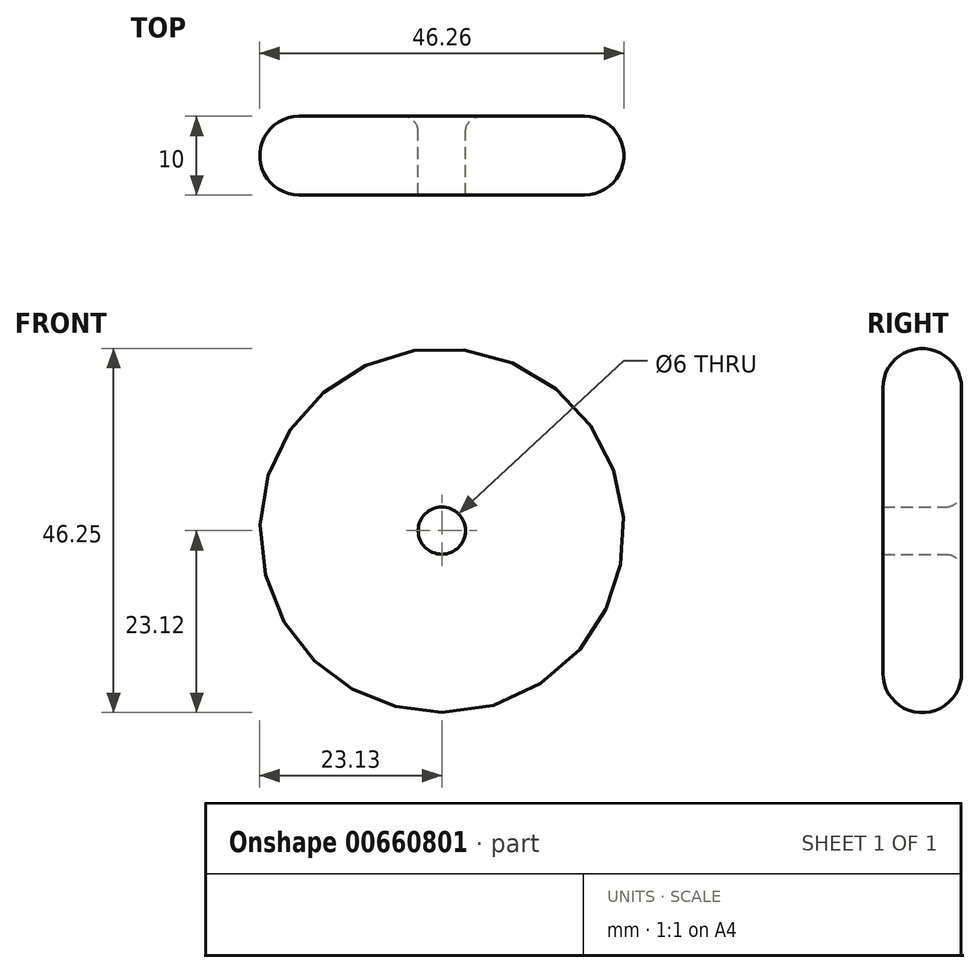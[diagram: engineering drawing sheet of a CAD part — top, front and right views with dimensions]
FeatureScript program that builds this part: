
annotation { "Feature Type Name" : "Feature", "Feature Type Description" : "" }
export const myFeature = defineFeature(function(context is Context, id is Id, definition is map)
    precondition{}
    {
        {
            var Q0;
            Q0=qCreatedBy(makeId("Front.planeOp"),FACE);
            var sketch = newSketch(context, id + "F0", { "sketchPlane" : qUnion([Q0])});
            skCircle(sketch, "E0", {"center": v(0, 0) * mm, "radius": 23.12 * mm});
            skCircle(sketch, "E1", {"center": v(0, 0) * mm, "radius": 3 * mm});
            skSolve(sketch);
        }
        {
            var Q0;
            Q0=makeQuery(id+"F0.imprint","IMPRINT",FACE,{"disambiguationData":[TD([[makeQuery(id+"F0.imprint","IMPRINT",EDGE,{"derivedFrom":sQuery(id+"F0.wireOp",EDGE,"E0")}),1.0]])]});
            extrude(context, id + "F1", {"entities" : qUnion([Q0]), "depth" : 10 * mm, "offsetDistance" : 25 * mm});
        }
        {
            var Q0;
            Q0=makeQuery(id+"F1.opExtrude","CAP_EDGE",EDGE,{"disambiguationData":[OSD([sQuery(id+"F0.wireOp",EDGE,"E0")])],"isStart":true});
            var Q1;
            Q1=makeQuery(id+"F1.opExtrude","CAP_EDGE",EDGE,{"disambiguationData":[OSD([sQuery(id+"F0.wireOp",EDGE,"E0")])],"isStart":false});
            fillet(context, id + "F2", {"entities" : qUnion([Q0, Q1]), "radius" : 5 * mm, "tangentPropagation" : true, "allowEdgeOverflow" : false});
        }
        {
            var Q0;
            Q0=makeQuery(id+"F1.opExtrude","CAP_EDGE",EDGE,{"disambiguationData":[OSD([sQuery(id+"F0.wireOp",EDGE,"E1")])],"isStart":true});
            var Q1;
            Q1=makeQuery(id+"F1.opExtrude","CAP_FACE",FACE,{"disambiguationData":[OSD([sQuery(id+"F0.wireOp",EDGE,"E0"),sQuery(id+"F0.wireOp",EDGE,"E1")])],"isStart":true});
            fillet(context, id + "F3", {"entities" : qUnion([Q0, Q1]), "radius" : 2 * mm, "tangentPropagation" : true, "allowEdgeOverflow" : false});
        }
    });
